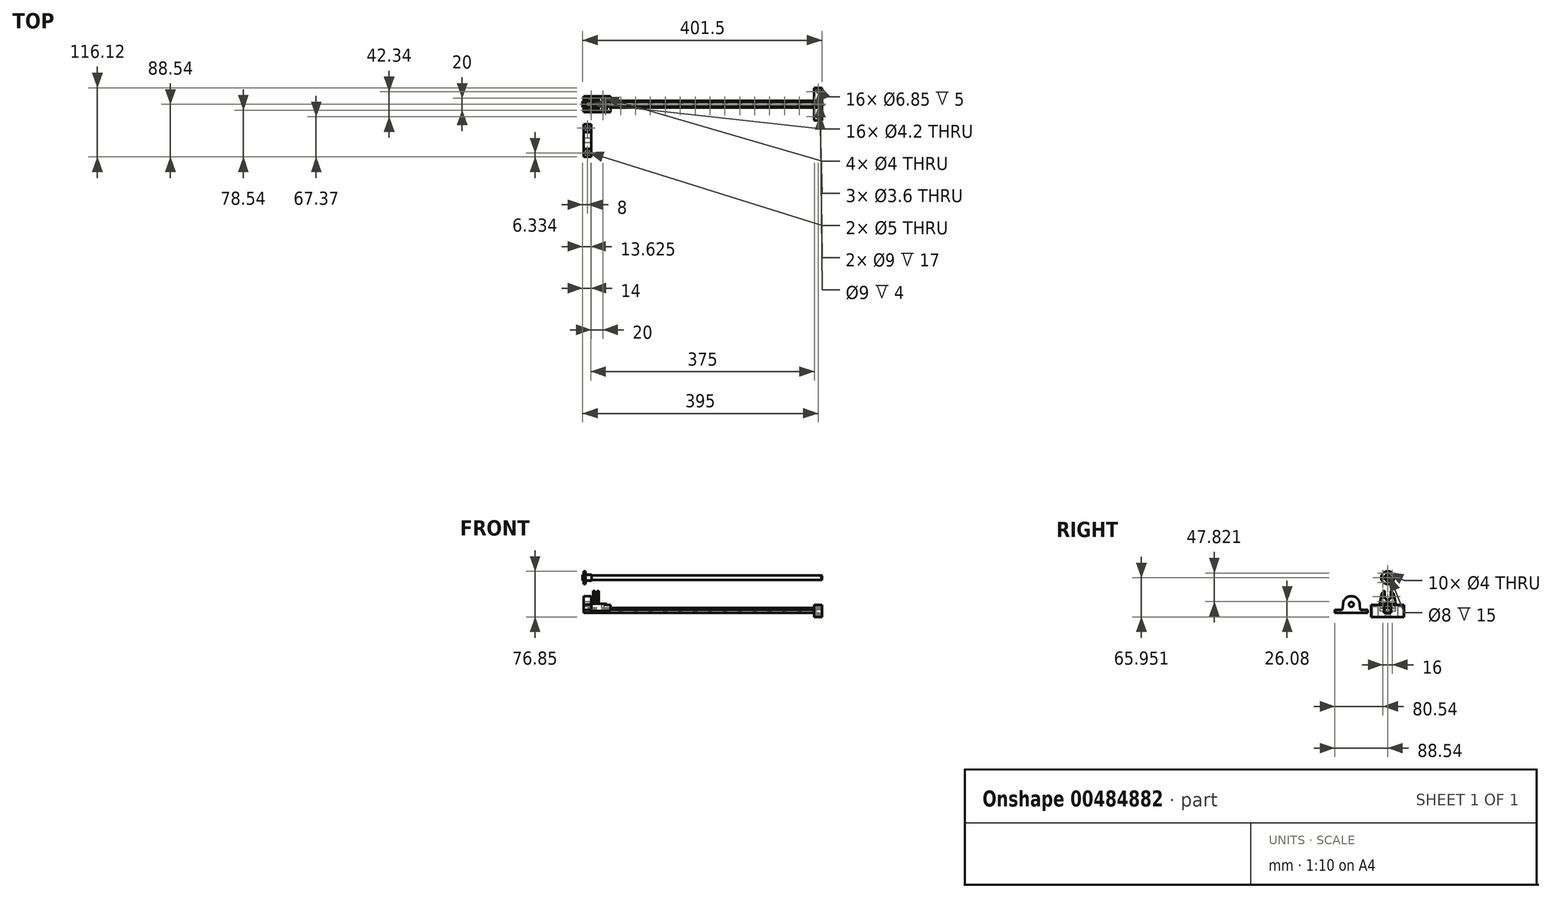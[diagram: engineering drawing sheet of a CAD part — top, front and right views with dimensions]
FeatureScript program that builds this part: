
annotation { "Feature Type Name" : "Feature", "Feature Type Description" : "" }
export const myFeature = defineFeature(function(context is Context, id is Id, definition is map)
    precondition{}
    {
        {
            var Q0;
            Q0=qCreatedBy(makeId("Right.planeOp"),FACE);
            var sketch = newSketch(context, id + "F0", { "sketchPlane" : qUnion([Q0])});
            skLineSegment(sketch, "E0.bottom", {"start": v(0, 0) * mm, "end": v(12, 0) * mm});
            skLineSegment(sketch, "E0.top", {"start": v(0, 8) * mm, "end": v(12, 8) * mm});
            skLineSegment(sketch, "E0.left", {"start": v(0, 0) * mm, "end": v(0, 8) * mm});
            skLineSegment(sketch, "E0.right", {"start": v(12, 0) * mm, "end": v(12, 8) * mm});
            skLineSegment(sketch, "E1", {"start": v(12, 0) * mm, "end": v(12, 3) * mm});
            skLineSegment(sketch, "E2", {"start": v(12, 3) * mm, "end": v(19.5, 3) * mm});
            skLineSegment(sketch, "E3", {"start": v(19.5, 3) * mm, "end": v(19.5, 13) * mm});
            skLineSegment(sketch, "E4", {"start": v(19.5, 13) * mm, "end": v(-7.5, 13) * mm});
            skLineSegment(sketch, "E5", {"start": v(-7.5, 13) * mm, "end": v(-7.5, 3) * mm});
            skLineSegment(sketch, "E6", {"start": v(-7.5, 3) * mm, "end": v(0, 3) * mm});
            skCircle(sketch, "E7", {"center": v(6, 58.87) * mm, "radius": 4 * mm});
            skCircle(sketch, "E8", {"center": v(6, 58.87) * mm, "radius": 10.9 * mm});
            skCircle(sketch, "E9", {"center": v(6, 58.87) * mm, "radius": 5 * mm});
            skLineSegment(sketch, "E10", {"start": v(1, 58.87) * mm, "end": v(-4.9, 58.87) * mm, "construction": true});
            skCircle(sketch, "E11", {"center": v(-1.95, 58.87) * mm, "radius": 2 * mm});
            skLineSegment(sketch, "E12", {"start": v(11, 58.87) * mm, "end": v(16.9, 58.87) * mm, "construction": true});
            skLineSegment(sketch, "E13", {"start": v(6, 53.87) * mm, "end": v(6, 47.97) * mm, "construction": true});
            skLineSegment(sketch, "E14", {"start": v(6, 63.87) * mm, "end": v(6, 69.77) * mm, "construction": true});
            skCircle(sketch, "E15", {"center": v(6, 66.82) * mm, "radius": 2 * mm});
            skCircle(sketch, "E16", {"center": v(13.95, 58.87) * mm, "radius": 2 * mm});
            skCircle(sketch, "E17", {"center": v(6, 50.92) * mm, "radius": 2 * mm});
            skLineSegment(sketch, "E18", {"start": v(-27.54, 0) * mm, "end": v(-82.54, 0) * mm});
            skLineSegment(sketch, "E19", {"start": v(-82.54, 0) * mm, "end": v(-82.54, 5) * mm});
            skLineSegment(sketch, "E20", {"start": v(-27.54, 0) * mm, "end": v(-27.54, 5) * mm});
            skLineSegment(sketch, "E21", {"start": v(-55.04, 0) * mm, "end": v(-55.04, 14) * mm, "construction": true});
            skPoint(sketch, "E21.endSnap0", {"position": v(-55.04, 0) * mm});
            skCircle(sketch, "E22", {"center": v(-55.04, 14) * mm, "radius": 14 * mm});
            skCircle(sketch, "E23", {"center": v(-55.04, 14) * mm, "radius": 4 * mm});
            skLineSegment(sketch, "E24", {"start": v(-40.2, 5) * mm, "end": v(-27.54, 5) * mm});
            skLineSegment(sketch, "E25", {"start": v(-69.88, 5) * mm, "end": v(-82.54, 5) * mm});
            skLineSegment(sketch, "E26", {"start": v(-41.04, 14) * mm, "end": v(-40.2, 5) * mm});
            skLineSegment(sketch, "E27", {"start": v(-69.04, 14) * mm, "end": v(-69.88, 5) * mm});
            skCircle(sketch, "E28", {"center": v(-55.04, 14) * mm, "radius": 5.9 * mm});
            skLineSegment(sketch, "E29", {"start": v(6, 0) * mm, "end": v(6, 58.87) * mm});
            skLineSegment(sketch, "E30", {"start": v(0, 6.36) * mm, "end": v(2, 5.52) * mm});
            skLineSegment(sketch, "E31", {"start": v(2, 5.52) * mm, "end": v(0, 4.68) * mm});
            skLineSegment(sketch, "E32.MirrorCS", {"start": v(12, 6.36) * mm, "end": v(10, 5.52) * mm});
            skLineSegment(sketch, "E33.MirrorCS", {"start": v(10, 5.52) * mm, "end": v(12, 4.68) * mm});
            skSolve(sketch);
        }
        {
            var Q0;
            {var subQ3=sQuery(id+"F0.wireOp",EDGE,"E0.bottom");Q0=makeQuery(id+"F0.imprint","IMPRINT",FACE,{"disambiguationData":[TD([[makeQuery(id+"F0.imprint","IMPRINT",EDGE,{"derivedFrom":subQ3}),1.0]])]});}
            extrude(context, id + "F1", {"entities" : qUnion([Q0]), "depth" : 400 * mm, "offsetDistance" : 25 * mm});
        }
        {
            var Q0;
            Q0=makeQuery(id+"F1.opExtrude","SWEPT_FACE",FACE,{"disambiguationData":[OSD([sQuery(id+"F0.wireOp",EDGE,"E0.top")])]});
            var sketch = newSketch(context, id + "F2", { "sketchPlane" : qUnion([Q0])});
            skLineSegment(sketch, "E34", {"start": v(0, 6) * mm, "end": v(12.12, 6) * mm, "construction": true});
            skCircle(sketch, "E35", {"center": v(12.12, 6) * mm, "radius": 3.43 * mm});
            skCircle(sketch, "E36", {"center": v(12.12, 6) * mm, "radius": 2.1 * mm});
            skCircle(sketch, "E37.1.0.0", {"center": v(37.13, 6) * mm, "radius": 2.1 * mm});
            skCircle(sketch, "E37.1.0.1", {"center": v(37.13, 6) * mm, "radius": 3.43 * mm});
            skCircle(sketch, "E37.2.0.0", {"center": v(62.13, 6) * mm, "radius": 2.1 * mm});
            skCircle(sketch, "E37.2.0.1", {"center": v(62.13, 6) * mm, "radius": 3.43 * mm});
            skCircle(sketch, "E37.3.0.0", {"center": v(87.13, 6) * mm, "radius": 2.1 * mm});
            skCircle(sketch, "E37.3.0.1", {"center": v(87.13, 6) * mm, "radius": 3.43 * mm});
            skCircle(sketch, "E37.4.0.0", {"center": v(112.13, 6) * mm, "radius": 2.1 * mm});
            skCircle(sketch, "E37.4.0.1", {"center": v(112.13, 6) * mm, "radius": 3.43 * mm});
            skCircle(sketch, "E37.5.0.0", {"center": v(137.13, 6) * mm, "radius": 2.1 * mm});
            skCircle(sketch, "E37.5.0.1", {"center": v(137.13, 6) * mm, "radius": 3.43 * mm});
            skCircle(sketch, "E37.6.0.0", {"center": v(162.13, 6) * mm, "radius": 2.1 * mm});
            skCircle(sketch, "E37.6.0.1", {"center": v(162.13, 6) * mm, "radius": 3.43 * mm});
            skCircle(sketch, "E37.7.0.0", {"center": v(187.13, 6) * mm, "radius": 2.1 * mm});
            skCircle(sketch, "E37.7.0.1", {"center": v(187.13, 6) * mm, "radius": 3.43 * mm});
            skCircle(sketch, "E37.8.0.0", {"center": v(212.13, 6) * mm, "radius": 2.1 * mm});
            skCircle(sketch, "E37.8.0.1", {"center": v(212.13, 6) * mm, "radius": 3.43 * mm});
            skCircle(sketch, "E37.9.0.0", {"center": v(237.13, 6) * mm, "radius": 2.1 * mm});
            skCircle(sketch, "E37.9.0.1", {"center": v(237.13, 6) * mm, "radius": 3.43 * mm});
            skCircle(sketch, "E37.10.0.0", {"center": v(262.13, 6) * mm, "radius": 2.1 * mm});
            skCircle(sketch, "E37.10.0.1", {"center": v(262.13, 6) * mm, "radius": 3.43 * mm});
            skCircle(sketch, "E37.11.0.0", {"center": v(287.13, 6) * mm, "radius": 2.1 * mm});
            skCircle(sketch, "E37.11.0.1", {"center": v(287.13, 6) * mm, "radius": 3.43 * mm});
            skCircle(sketch, "E37.12.0.0", {"center": v(312.13, 6) * mm, "radius": 2.1 * mm});
            skCircle(sketch, "E37.12.0.1", {"center": v(312.13, 6) * mm, "radius": 3.43 * mm});
            skCircle(sketch, "E37.13.0.0", {"center": v(337.13, 6) * mm, "radius": 2.1 * mm});
            skCircle(sketch, "E37.13.0.1", {"center": v(337.13, 6) * mm, "radius": 3.43 * mm});
            skCircle(sketch, "E37.14.0.0", {"center": v(362.13, 6) * mm, "radius": 2.1 * mm});
            skCircle(sketch, "E37.14.0.1", {"center": v(362.13, 6) * mm, "radius": 3.43 * mm});
            skCircle(sketch, "E37.15.0.0", {"center": v(387.13, 6) * mm, "radius": 2.1 * mm});
            skCircle(sketch, "E37.15.0.1", {"center": v(387.13, 6) * mm, "radius": 3.43 * mm});
            skLineSegment(sketch, "E37.direction1", {"start": v(12.12, 6) * mm, "end": v(37.13, 6) * mm, "construction": true});
            skLineSegment(sketch, "E38", {"start": v(112.13, 6) * mm, "end": v(87.13, 6) * mm});
            skSolve(sketch);
        }
        {
            var Q0;
            Q0=makeQuery(id+"F2.imprint","IMPRINT",FACE,{"disambiguationData":[TD([[makeQuery(id+"F2.imprint","IMPRINT",EDGE,{"derivedFrom":sQuery(id+"F2.wireOp",EDGE,"E35")}),1.0]])]});
            var Q1;
            Q1=makeQuery(id+"F2.imprint","IMPRINT",FACE,{"disambiguationData":[TD([[makeQuery(id+"F2.imprint","IMPRINT",EDGE,{"derivedFrom":sQuery(id+"F2.wireOp",EDGE,"E36")}),1.0]])]});
            var Q2;
            Q2=makeQuery(id+"F2.imprint","IMPRINT",FACE,{"disambiguationData":[TD([[makeQuery(id+"F2.imprint","IMPRINT",EDGE,{"derivedFrom":sQuery(id+"F2.wireOp",EDGE,"E37.1.0.0")}),1.0]])]});
            var Q3;
            Q3=makeQuery(id+"F2.imprint","IMPRINT",FACE,{"disambiguationData":[TD([[makeQuery(id+"F2.imprint","IMPRINT",EDGE,{"derivedFrom":sQuery(id+"F2.wireOp",EDGE,"E37.1.0.0")}),-1.0]])]});
            var Q4;
            Q4=makeQuery(id+"F2.imprint","IMPRINT",FACE,{"disambiguationData":[TD([[makeQuery(id+"F2.imprint","IMPRINT",EDGE,{"derivedFrom":sQuery(id+"F2.wireOp",EDGE,"E37.2.0.0")}),1.0]])]});
            var Q5;
            Q5=makeQuery(id+"F2.imprint","IMPRINT",FACE,{"disambiguationData":[TD([[makeQuery(id+"F2.imprint","IMPRINT",EDGE,{"derivedFrom":sQuery(id+"F2.wireOp",EDGE,"E37.2.0.0")}),-1.0]])]});
            var Q6;
            Q6=makeQuery(id+"F2.imprint","IMPRINT",FACE,{"disambiguationData":[TD([[makeQuery(id+"F2.imprint","IMPRINT",EDGE,{"derivedFrom":sQuery(id+"F2.wireOp",EDGE,"E37.3.0.0")}),1.0]])]});
            var Q7;
            Q7=makeQuery(id+"F2.imprint","IMPRINT",FACE,{"disambiguationData":[TD([[makeQuery(id+"F2.imprint","IMPRINT",EDGE,{"derivedFrom":sQuery(id+"F2.wireOp",EDGE,"E37.3.0.0")}),-1.0]])]});
            var Q8;
            Q8=makeQuery(id+"F2.imprint","IMPRINT",FACE,{"disambiguationData":[TD([[makeQuery(id+"F2.imprint","IMPRINT",EDGE,{"derivedFrom":sQuery(id+"F2.wireOp",EDGE,"E37.4.0.0")}),1.0]])]});
            var Q9;
            Q9=makeQuery(id+"F2.imprint","IMPRINT",FACE,{"disambiguationData":[TD([[makeQuery(id+"F2.imprint","IMPRINT",EDGE,{"derivedFrom":sQuery(id+"F2.wireOp",EDGE,"E37.4.0.0")}),-1.0]])]});
            var Q10;
            Q10=makeQuery(id+"F2.imprint","IMPRINT",FACE,{"disambiguationData":[TD([[makeQuery(id+"F2.imprint","IMPRINT",EDGE,{"derivedFrom":sQuery(id+"F2.wireOp",EDGE,"E37.5.0.0")}),1.0]])]});
            var Q11;
            Q11=makeQuery(id+"F2.imprint","IMPRINT",FACE,{"disambiguationData":[TD([[makeQuery(id+"F2.imprint","IMPRINT",EDGE,{"derivedFrom":sQuery(id+"F2.wireOp",EDGE,"E37.5.0.0")}),-1.0]])]});
            var Q12;
            Q12=makeQuery(id+"F2.imprint","IMPRINT",FACE,{"disambiguationData":[TD([[makeQuery(id+"F2.imprint","IMPRINT",EDGE,{"derivedFrom":sQuery(id+"F2.wireOp",EDGE,"E37.6.0.0")}),1.0]])]});
            var Q13;
            Q13=makeQuery(id+"F2.imprint","IMPRINT",FACE,{"disambiguationData":[TD([[makeQuery(id+"F2.imprint","IMPRINT",EDGE,{"derivedFrom":sQuery(id+"F2.wireOp",EDGE,"E37.6.0.0")}),-1.0]])]});
            var Q14;
            Q14=makeQuery(id+"F2.imprint","IMPRINT",FACE,{"disambiguationData":[TD([[makeQuery(id+"F2.imprint","IMPRINT",EDGE,{"derivedFrom":sQuery(id+"F2.wireOp",EDGE,"E37.7.0.0")}),1.0]])]});
            var Q15;
            Q15=makeQuery(id+"F2.imprint","IMPRINT",FACE,{"disambiguationData":[TD([[makeQuery(id+"F2.imprint","IMPRINT",EDGE,{"derivedFrom":sQuery(id+"F2.wireOp",EDGE,"E37.7.0.0")}),-1.0]])]});
            var Q16;
            Q16=makeQuery(id+"F2.imprint","IMPRINT",FACE,{"disambiguationData":[TD([[makeQuery(id+"F2.imprint","IMPRINT",EDGE,{"derivedFrom":sQuery(id+"F2.wireOp",EDGE,"E37.15.0.0")}),1.0]])]});
            var Q17;
            Q17=makeQuery(id+"F2.imprint","IMPRINT",FACE,{"disambiguationData":[TD([[makeQuery(id+"F2.imprint","IMPRINT",EDGE,{"derivedFrom":sQuery(id+"F2.wireOp",EDGE,"E37.15.0.0")}),-1.0]])]});
            var Q18;
            Q18=makeQuery(id+"F2.imprint","IMPRINT",FACE,{"disambiguationData":[TD([[makeQuery(id+"F2.imprint","IMPRINT",EDGE,{"derivedFrom":sQuery(id+"F2.wireOp",EDGE,"E37.14.0.0")}),1.0]])]});
            var Q19;
            Q19=makeQuery(id+"F2.imprint","IMPRINT",FACE,{"disambiguationData":[TD([[makeQuery(id+"F2.imprint","IMPRINT",EDGE,{"derivedFrom":sQuery(id+"F2.wireOp",EDGE,"E37.14.0.0")}),-1.0]])]});
            var Q20;
            Q20=makeQuery(id+"F2.imprint","IMPRINT",FACE,{"disambiguationData":[TD([[makeQuery(id+"F2.imprint","IMPRINT",EDGE,{"derivedFrom":sQuery(id+"F2.wireOp",EDGE,"E37.13.0.0")}),1.0]])]});
            var Q21;
            Q21=makeQuery(id+"F2.imprint","IMPRINT",FACE,{"disambiguationData":[TD([[makeQuery(id+"F2.imprint","IMPRINT",EDGE,{"derivedFrom":sQuery(id+"F2.wireOp",EDGE,"E37.13.0.0")}),-1.0]])]});
            var Q22;
            Q22=makeQuery(id+"F2.imprint","IMPRINT",FACE,{"disambiguationData":[TD([[makeQuery(id+"F2.imprint","IMPRINT",EDGE,{"derivedFrom":sQuery(id+"F2.wireOp",EDGE,"E37.12.0.0")}),1.0]])]});
            var Q23;
            Q23=makeQuery(id+"F2.imprint","IMPRINT",FACE,{"disambiguationData":[TD([[makeQuery(id+"F2.imprint","IMPRINT",EDGE,{"derivedFrom":sQuery(id+"F2.wireOp",EDGE,"E37.12.0.0")}),-1.0]])]});
            var Q24;
            Q24=makeQuery(id+"F2.imprint","IMPRINT",FACE,{"disambiguationData":[TD([[makeQuery(id+"F2.imprint","IMPRINT",EDGE,{"derivedFrom":sQuery(id+"F2.wireOp",EDGE,"E37.11.0.0")}),1.0]])]});
            var Q25;
            Q25=makeQuery(id+"F2.imprint","IMPRINT",FACE,{"disambiguationData":[TD([[makeQuery(id+"F2.imprint","IMPRINT",EDGE,{"derivedFrom":sQuery(id+"F2.wireOp",EDGE,"E37.11.0.0")}),-1.0]])]});
            var Q26;
            Q26=makeQuery(id+"F2.imprint","IMPRINT",FACE,{"disambiguationData":[TD([[makeQuery(id+"F2.imprint","IMPRINT",EDGE,{"derivedFrom":sQuery(id+"F2.wireOp",EDGE,"E37.10.0.0")}),1.0]])]});
            var Q27;
            Q27=makeQuery(id+"F2.imprint","IMPRINT",FACE,{"disambiguationData":[TD([[makeQuery(id+"F2.imprint","IMPRINT",EDGE,{"derivedFrom":sQuery(id+"F2.wireOp",EDGE,"E37.10.0.0")}),-1.0]])]});
            var Q28;
            Q28=makeQuery(id+"F2.imprint","IMPRINT",FACE,{"disambiguationData":[TD([[makeQuery(id+"F2.imprint","IMPRINT",EDGE,{"derivedFrom":sQuery(id+"F2.wireOp",EDGE,"E37.9.0.0")}),1.0]])]});
            var Q29;
            Q29=makeQuery(id+"F2.imprint","IMPRINT",FACE,{"disambiguationData":[TD([[makeQuery(id+"F2.imprint","IMPRINT",EDGE,{"derivedFrom":sQuery(id+"F2.wireOp",EDGE,"E37.9.0.0")}),-1.0]])]});
            var Q30;
            Q30=makeQuery(id+"F2.imprint","IMPRINT",FACE,{"disambiguationData":[TD([[makeQuery(id+"F2.imprint","IMPRINT",EDGE,{"derivedFrom":sQuery(id+"F2.wireOp",EDGE,"E37.8.0.0")}),1.0]])]});
            var Q31;
            Q31=makeQuery(id+"F2.imprint","IMPRINT",FACE,{"disambiguationData":[TD([[makeQuery(id+"F2.imprint","IMPRINT",EDGE,{"derivedFrom":sQuery(id+"F2.wireOp",EDGE,"E37.8.0.0")}),-1.0]])]});
            extrude(context, id + "F3", {"entities" : qUnion([Q0, Q1, Q2, Q3, Q4, Q5, Q6, Q7, Q8, Q9, Q10, Q11, Q12, Q13, Q14, Q15, Q16, Q17, Q18, Q19, Q20, Q21, Q22, Q23, Q24, Q25, Q26, Q27, Q28, Q29, Q30, Q31]), "operationType" : NewBodyOperationType.REMOVE, "oppositeDirection" : true, "depth" : 5 * mm, "offsetDistance" : 25 * mm});
        }
        {
            var Q0;
            Q0=makeQuery(id+"F2.imprint","IMPRINT",FACE,{"disambiguationData":[TD([[makeQuery(id+"F2.imprint","IMPRINT",EDGE,{"derivedFrom":sQuery(id+"F2.wireOp",EDGE,"E36")}),1.0]])]});
            var Q1;
            Q1=makeQuery(id+"F2.imprint","IMPRINT",FACE,{"disambiguationData":[TD([[makeQuery(id+"F2.imprint","IMPRINT",EDGE,{"derivedFrom":sQuery(id+"F2.wireOp",EDGE,"E37.1.0.0")}),1.0]])]});
            var Q2;
            Q2=makeQuery(id+"F2.imprint","IMPRINT",FACE,{"disambiguationData":[TD([[makeQuery(id+"F2.imprint","IMPRINT",EDGE,{"derivedFrom":sQuery(id+"F2.wireOp",EDGE,"E37.2.0.0")}),1.0]])]});
            var Q3;
            Q3=makeQuery(id+"F2.imprint","IMPRINT",FACE,{"disambiguationData":[TD([[makeQuery(id+"F2.imprint","IMPRINT",EDGE,{"derivedFrom":sQuery(id+"F2.wireOp",EDGE,"E37.3.0.0")}),1.0]])]});
            var Q4;
            Q4=makeQuery(id+"F2.imprint","IMPRINT",FACE,{"disambiguationData":[TD([[makeQuery(id+"F2.imprint","IMPRINT",EDGE,{"derivedFrom":sQuery(id+"F2.wireOp",EDGE,"E37.4.0.0")}),1.0]])]});
            var Q5;
            Q5=makeQuery(id+"F2.imprint","IMPRINT",FACE,{"disambiguationData":[TD([[makeQuery(id+"F2.imprint","IMPRINT",EDGE,{"derivedFrom":sQuery(id+"F2.wireOp",EDGE,"E37.5.0.0")}),1.0]])]});
            var Q6;
            Q6=makeQuery(id+"F2.imprint","IMPRINT",FACE,{"disambiguationData":[TD([[makeQuery(id+"F2.imprint","IMPRINT",EDGE,{"derivedFrom":sQuery(id+"F2.wireOp",EDGE,"E37.6.0.0")}),1.0]])]});
            var Q7;
            Q7=makeQuery(id+"F2.imprint","IMPRINT",FACE,{"disambiguationData":[TD([[makeQuery(id+"F2.imprint","IMPRINT",EDGE,{"derivedFrom":sQuery(id+"F2.wireOp",EDGE,"E37.7.0.0")}),1.0]])]});
            var Q8;
            Q8=makeQuery(id+"F2.imprint","IMPRINT",FACE,{"disambiguationData":[TD([[makeQuery(id+"F2.imprint","IMPRINT",EDGE,{"derivedFrom":sQuery(id+"F2.wireOp",EDGE,"E37.8.0.0")}),1.0]])]});
            var Q9;
            Q9=makeQuery(id+"F2.imprint","IMPRINT",FACE,{"disambiguationData":[TD([[makeQuery(id+"F2.imprint","IMPRINT",EDGE,{"derivedFrom":sQuery(id+"F2.wireOp",EDGE,"E37.9.0.0")}),1.0]])]});
            var Q10;
            Q10=makeQuery(id+"F2.imprint","IMPRINT",FACE,{"disambiguationData":[TD([[makeQuery(id+"F2.imprint","IMPRINT",EDGE,{"derivedFrom":sQuery(id+"F2.wireOp",EDGE,"E37.10.0.0")}),1.0]])]});
            var Q11;
            Q11=makeQuery(id+"F2.imprint","IMPRINT",FACE,{"disambiguationData":[TD([[makeQuery(id+"F2.imprint","IMPRINT",EDGE,{"derivedFrom":sQuery(id+"F2.wireOp",EDGE,"E37.11.0.0")}),1.0]])]});
            var Q12;
            Q12=makeQuery(id+"F2.imprint","IMPRINT",FACE,{"disambiguationData":[TD([[makeQuery(id+"F2.imprint","IMPRINT",EDGE,{"derivedFrom":sQuery(id+"F2.wireOp",EDGE,"E37.12.0.0")}),1.0]])]});
            var Q13;
            Q13=makeQuery(id+"F2.imprint","IMPRINT",FACE,{"disambiguationData":[TD([[makeQuery(id+"F2.imprint","IMPRINT",EDGE,{"derivedFrom":sQuery(id+"F2.wireOp",EDGE,"E37.13.0.0")}),1.0]])]});
            var Q14;
            Q14=makeQuery(id+"F2.imprint","IMPRINT",FACE,{"disambiguationData":[TD([[makeQuery(id+"F2.imprint","IMPRINT",EDGE,{"derivedFrom":sQuery(id+"F2.wireOp",EDGE,"E37.14.0.0")}),1.0]])]});
            var Q15;
            Q15=makeQuery(id+"F2.imprint","IMPRINT",FACE,{"disambiguationData":[TD([[makeQuery(id+"F2.imprint","IMPRINT",EDGE,{"derivedFrom":sQuery(id+"F2.wireOp",EDGE,"E37.15.0.0")}),1.0]])]});
            var Q16;
            Q16=makeQuery(id+"F1.opExtrude","SWEPT_FACE",FACE,{"disambiguationData":[OSD([sQuery(id+"F0.wireOp",EDGE,"E0.bottom")])]});
            extrude(context, id + "F4", {"entities" : qUnion([Q0, Q1, Q2, Q3, Q4, Q5, Q6, Q7, Q8, Q9, Q10, Q11, Q12, Q13, Q14, Q15]), "operationType" : NewBodyOperationType.REMOVE, "endBound" : BoundingType.UP_TO_SURFACE, "oppositeDirection" : true, "depth" : 25 * mm, "endBoundEntityFace" : qUnion([Q16]), "offsetDistance" : 25 * mm});
        }
        {
            var Q0;
            {var subQ1=sQuery(id+"F0.wireOp",EDGE,"E0.top");Q0=makeQuery(id+"F0.imprint","IMPRINT",FACE,{"disambiguationData":[TD([[makeQuery(id+"F0.imprint","IMPRINT",EDGE,{"derivedFrom":subQ1}),1.0]])]});}
            var Q1;
            {var subQ0=sQuery(id+"F0.wireOp",EDGE,"E30");Q1=makeQuery(id+"F0.imprint","IMPRINT",FACE,{"disambiguationData":[TD([[makeQuery(id+"F0.imprint","IMPRINT",EDGE,{"derivedFrom":subQ0}),-1.0]])]});}
            var Q2;
            {var subQ0=sQuery(id+"F0.wireOp",EDGE,"E32.MirrorCS");Q2=makeQuery(id+"F0.imprint","IMPRINT",FACE,{"disambiguationData":[TD([[makeQuery(id+"F0.imprint","IMPRINT",EDGE,{"derivedFrom":subQ0}),1.0]])]});}
            extrude(context, id + "F5", {"entities" : qUnion([Q0, Q1, Q2]), "depth" : 45 * mm, "offsetDistance" : 25 * mm});
        }
        {
            var Q0;
            Q0=makeQuery(id+"F5.opExtrude","SWEPT_FACE",FACE,{"disambiguationData":[OSD([sQuery(id+"F0.wireOp",EDGE,"E4")])]});
            var sketch = newSketch(context, id + "F6", { "sketchPlane" : qUnion([Q0])});
            skLineSegment(sketch, "E39", {"start": v(11.25, 19.5) * mm, "end": v(12.5, 19.5) * mm});
            skLineSegment(sketch, "E40", {"start": v(12.5, 19.5) * mm, "end": v(12.5, 16) * mm, "construction": true});
            skLineSegment(sketch, "E41", {"start": v(12.5, 16) * mm, "end": v(32.5, 16) * mm, "construction": true});
            skLineSegment(sketch, "E42", {"start": v(32.5, 16) * mm, "end": v(32.5, -4) * mm, "construction": true});
            skLineSegment(sketch, "E43", {"start": v(32.5, -4) * mm, "end": v(12.5, -4) * mm, "construction": true});
            skLineSegment(sketch, "E44", {"start": v(32.5, 16) * mm, "end": v(45, 16) * mm});
            skCircle(sketch, "E45", {"center": v(12.5, 16) * mm, "radius": 2 * mm});
            skCircle(sketch, "E46", {"center": v(32.5, 16) * mm, "radius": 2 * mm});
            skCircle(sketch, "E47", {"center": v(32.5, -4) * mm, "radius": 2 * mm});
            skCircle(sketch, "E48", {"center": v(12.5, -4) * mm, "radius": 2 * mm});
            skLineSegment(sketch, "E49", {"start": v(6.25, 14.5) * mm, "end": v(6.25, -2.5) * mm});
            skLineSegment(sketch, "E50", {"start": v(38.75, 14.5) * mm, "end": v(38.75, -2.5) * mm});
            skPoint(sketch, "E50.startSnap0", {"position": v(38.75, 16) * mm});
            skLineSegment(sketch, "E51", {"start": v(33.75, 19.5) * mm, "end": v(12.5, 19.5) * mm});
            skLineSegment(sketch, "E52", {"start": v(33.75, -7.5) * mm, "end": v(11.25, -7.5) * mm});
            skPoint(sketch, "E53.newPointA", {"position": v(6.25, 19.5) * mm});
            skPoint(sketch, "E53.newPointB", {"position": v(0, 19.5) * mm});
            skArc(sketch, "E53.filletArc", {"start": v(11.25, 19.5) * mm, "mid": v(7.71, 18.04) * mm, "end": v(6.25, 14.5) * mm});
            skPoint(sketch, "E54.visualSharp", {"position": v(6.25, -7.5) * mm});
            skArc(sketch, "E54.filletArc", {"start": v(6.25, -2.5) * mm, "mid": v(7.71, -6.04) * mm, "end": v(11.25, -7.5) * mm});
            skPoint(sketch, "E55.visualSharp", {"position": v(38.75, -7.5) * mm});
            skArc(sketch, "E55.filletArc", {"start": v(33.75, -7.5) * mm, "mid": v(37.29, -6.04) * mm, "end": v(38.75, -2.5) * mm});
            skPoint(sketch, "E56.visualSharp", {"position": v(38.75, 19.5) * mm});
            skArc(sketch, "E56.filletArc", {"start": v(38.75, 14.5) * mm, "mid": v(37.29, 18.04) * mm, "end": v(33.75, 19.5) * mm});
            skLineSegment(sketch, "E57", {"start": v(16.25, 19.5) * mm, "end": v(16.25, -7.5) * mm});
            skLineSegment(sketch, "E58", {"start": v(19.25, 19.5) * mm, "end": v(19.25, -7.5) * mm});
            skLineSegment(sketch, "E59", {"start": v(25.75, 19.5) * mm, "end": v(25.75, -7.5) * mm});
            skLineSegment(sketch, "E60", {"start": v(22.75, -7.5) * mm, "end": v(22.75, 19.5) * mm});
            skLineSegment(sketch, "E61", {"start": v(19.25, 6) * mm, "end": v(22.75, 6) * mm, "construction": true});
            skLineSegment(sketch, "E62", {"start": v(19.25, 6) * mm, "end": v(16.25, 6) * mm, "construction": true});
            skLineSegment(sketch, "E63", {"start": v(22.75, 6) * mm, "end": v(25.75, 6) * mm, "construction": true});
            skLineSegment(sketch, "E64", {"start": v(16.25, 6) * mm, "end": v(6.25, 6) * mm, "construction": true});
            skSolve(sketch);
        }
        {
            var Q0;
            Q0=sQuery(id+"F6.wireOp",VERTEX,"E41.start");
            var Q1;
            Q1=sQuery(id+"F6.wireOp",VERTEX,"E42.start");
            var Q2;
            Q2=sQuery(id+"F6.wireOp",VERTEX,"E42.end");
            var Q3;
            Q3=sQuery(id+"F6.wireOp",VERTEX,"E43.end");
            var Q4;
            Q4=makeQuery(id+"F5.opExtrude","SWEPT_BODY",BODY,{"disambiguationData":[OSD([sQuery(id+"F0.wireOp",EDGE,"E0.top"),sQuery(id+"F0.wireOp",EDGE,"E0.left"),sQuery(id+"F0.wireOp",EDGE,"E0.right"),sQuery(id+"F0.wireOp",EDGE,"E2"),sQuery(id+"F0.wireOp",EDGE,"E3"),sQuery(id+"F0.wireOp",EDGE,"E4"),sQuery(id+"F0.wireOp",EDGE,"E5"),sQuery(id+"F0.wireOp",EDGE,"E6")])]});
            hole(context, id + "F7", {"style" : HoleStyle.SIMPLE, "endStyle" : HoleEndStyle.BLIND, "holeDiameter" : 4 * mm, "majorDiameter" : 5 * mm, "holeDepth" : 5 * mm, "isTappedThrough" : true, "tappedDepth" : 12 * mm, "tapClearance" : 3, "locations" : qUnion([Q0, Q1, Q2, Q3]), "scope" : qUnion([Q4])});
        }
        {
            var Q0;
            Q0 = qSketchRegion(id + "F6", true);
            extrude(context, id + "F8", {"entities" : qUnion([Q0]), "depth" : 2 * mm, "offsetDistance" : 25 * mm});
        }
        {
            var Q0;
            {var subQ0=sQuery(id+"F6.wireOp",EDGE,"E59");Q0=makeQuery(id+"F6.imprint","IMPRINT",FACE,{"disambiguationData":[TD([[makeQuery(id+"F6.imprint","IMPRINT",EDGE,{"derivedFrom":subQ0}),-1.0]])]});}
            var Q1;
            {var subQ0=sQuery(id+"F6.wireOp",EDGE,"E57");Q1=makeQuery(id+"F6.imprint","IMPRINT",FACE,{"disambiguationData":[TD([[makeQuery(id+"F6.imprint","IMPRINT",EDGE,{"derivedFrom":subQ0}),1.0]])]});}
            extrude(context, id + "F9", {"entities" : qUnion([Q0, Q1]), "operationType" : NewBodyOperationType.ADD, "depth" : 26 * mm, "offsetDistance" : 25 * mm});
        }
        {
            var Q0;
            Q0=makeQuery(id+"F9.opExtrude","SWEPT_FACE",FACE,{"disambiguationData":[OSD([sQuery(id+"F6.wireOp",EDGE,"E59")])]});
            var sketch = newSketch(context, id + "F10", { "sketchPlane" : qUnion([Q0])});
            skLineSegment(sketch, "E65", {"start": v(6, 15) * mm, "end": v(6, 27) * mm, "construction": true});
            skCircle(sketch, "E66", {"center": v(6, 27) * mm, "radius": 5 * mm});
            skCircle(sketch, "E67", {"center": v(6, 27) * mm, "radius": 11 * mm});
            skLineSegment(sketch, "E68", {"start": v(1, 27) * mm, "end": v(1, 39) * mm});
            skLineSegment(sketch, "E69", {"start": v(11, 27) * mm, "end": v(11, 39) * mm});
            skLineSegment(sketch, "E70", {"start": v(-7.5, 15) * mm, "end": v(-4.8, 29.07) * mm});
            skLineSegment(sketch, "E71", {"start": v(19.5, 15) * mm, "end": v(16.8, 29.07) * mm});
            skLineSegment(sketch, "E72", {"start": v(1, 27) * mm, "end": v(-5, 27) * mm, "construction": true});
            skLineSegment(sketch, "E73", {"start": v(11, 27) * mm, "end": v(17, 27) * mm, "construction": true});
            skLineSegment(sketch, "E74", {"start": v(6, 22) * mm, "end": v(6, 16) * mm, "construction": true});
            skLineSegment(sketch, "E75", {"start": v(6, 32) * mm, "end": v(6, 38) * mm, "construction": true});
            skCircle(sketch, "E76", {"center": v(-2, 27) * mm, "radius": 2 * mm});
            skCircle(sketch, "E77", {"center": v(6, 35) * mm, "radius": 2 * mm});
            skCircle(sketch, "E78", {"center": v(6, 19) * mm, "radius": 2 * mm});
            skCircle(sketch, "E79", {"center": v(14, 27) * mm, "radius": 2 * mm});
            skSolve(sketch);
        }
        {
            var Q0;
            {var subQ0=sQuery(id+"F10.wireOp",EDGE,"E68");var subQ1=sQuery(id+"F10.wireOp",EDGE,"E66");var subQ2=makeQuery(id+"F10.imprint","INTERSECT",VERTEX,{"derivedFrom":[subQ1,subQ0]});Q0=makeQuery(id+"F10.imprint","IMPRINT",FACE,{"disambiguationData":[TD([[makeQuery(id+"F10.imprint","IMPRINT",EDGE,{"disambiguationData":[TD([[subQ2,1.0]])],"derivedFrom":subQ1}),-1.0]])]});}
            var Q1;
            {var subQ0=sQuery(id+"F10.wireOp",EDGE,"E68");var subQ1=sQuery(id+"F10.wireOp",EDGE,"E67");var subQ2=makeQuery(id+"F10.imprint","INTERSECT",VERTEX,{"derivedFrom":[subQ1,subQ0]});Q1=makeQuery(id+"F10.imprint","IMPRINT",FACE,{"disambiguationData":[TD([[makeQuery(id+"F10.imprint","IMPRINT",EDGE,{"disambiguationData":[TD([[subQ2,1.0]])],"derivedFrom":subQ1}),-1.0]])]});}
            var Q2;
            {var subQ0=sQuery(id+"F10.wireOp",EDGE,"E66");var subQ1=makeQuery(id+"F10.imprint","INTERSECT",VERTEX,{"derivedFrom":[subQ0,sQuery(id+"F10.wireOp",EDGE,"E68")]});Q2=makeQuery(id+"F10.imprint","IMPRINT",FACE,{"disambiguationData":[TD([[makeQuery(id+"F10.imprint","IMPRINT",EDGE,{"disambiguationData":[TD([[subQ1,1.0]])],"derivedFrom":subQ0}),1.0]])]});}
            var Q3;
            {var subQ2=sQuery(id+"F10.wireOp",EDGE,"E70");Q3=makeQuery(id+"F10.imprint","IMPRINT",FACE,{"disambiguationData":[TD([[makeQuery(id+"F10.imprint","IMPRINT",EDGE,{"derivedFrom":subQ2}),1.0]])]});}
            var Q4;
            {var subQ0=sQuery(id+"F10.wireOp",EDGE,"E71");Q4=makeQuery(id+"F10.imprint","IMPRINT",FACE,{"disambiguationData":[TD([[makeQuery(id+"F10.imprint","IMPRINT",EDGE,{"derivedFrom":subQ0}),-1.0]])]});}
            var Q5;
            Q5=makeQuery(id+"F10.imprint","IMPRINT",FACE,{"disambiguationData":[TD([[makeQuery(id+"F10.imprint","IMPRINT",EDGE,{"derivedFrom":sQuery(id+"F10.wireOp",EDGE,"E77")}),1.0]])]});
            var Q6;
            Q6=makeQuery(id+"F10.imprint","IMPRINT",FACE,{"disambiguationData":[TD([[makeQuery(id+"F10.imprint","IMPRINT",EDGE,{"derivedFrom":sQuery(id+"F10.wireOp",EDGE,"E79")}),1.0]])]});
            var Q7;
            Q7=makeQuery(id+"F10.imprint","IMPRINT",FACE,{"disambiguationData":[TD([[makeQuery(id+"F10.imprint","IMPRINT",EDGE,{"derivedFrom":sQuery(id+"F10.wireOp",EDGE,"E78")}),1.0]])]});
            var Q8;
            Q8=makeQuery(id+"F10.imprint","IMPRINT",FACE,{"disambiguationData":[TD([[makeQuery(id+"F10.imprint","IMPRINT",EDGE,{"derivedFrom":sQuery(id+"F10.wireOp",EDGE,"E76")}),1.0]])]});
            var Q9;
            Q9=makeQuery(id+"F9.opExtrude","SWEPT_FACE",FACE,{"disambiguationData":[OSD([sQuery(id+"F6.wireOp",EDGE,"E57")])]});
            extrude(context, id + "F11", {"entities" : qUnion([Q0, Q1, Q2, Q3, Q4, Q5, Q6, Q7, Q8]), "operationType" : NewBodyOperationType.REMOVE, "endBound" : BoundingType.UP_TO_SURFACE, "oppositeDirection" : true, "depth" : 25 * mm, "endBoundEntityFace" : qUnion([Q9]), "offsetDistance" : 25 * mm});
        }
        {
            var Q0;
            Q0=makeQuery(id+"F0.imprint","IMPRINT",FACE,{"disambiguationData":[TD([[makeQuery(id+"F0.imprint","IMPRINT",EDGE,{"derivedFrom":sQuery(id+"F0.wireOp",EDGE,"E7")}),-1.0]])]});
            extrude(context, id + "F12", {"entities" : qUnion([Q0]), "oppositeDirection" : true, "depth" : 1.5 * mm, "offsetDistance" : 25 * mm});
        }
        {
            var Q0;
            Q0=makeQuery(id+"F0.imprint","IMPRINT",FACE,{"disambiguationData":[TD([[makeQuery(id+"F0.imprint","IMPRINT",EDGE,{"derivedFrom":sQuery(id+"F0.wireOp",EDGE,"E7")}),-1.0]])]});
            extrude(context, id + "F13", {"entities" : qUnion([Q0]), "operationType" : NewBodyOperationType.ADD, "depth" : 13.5 * mm, "offsetDistance" : 25 * mm});
        }
        {
            var Q0;
            Q0=makeQuery(id+"F0.imprint","IMPRINT",FACE,{"disambiguationData":[TD([[makeQuery(id+"F0.imprint","IMPRINT",EDGE,{"derivedFrom":sQuery(id+"F0.wireOp",EDGE,"E8")}),1.0]])]});
            extrude(context, id + "F14", {"entities" : qUnion([Q0]), "operationType" : NewBodyOperationType.ADD, "depth" : 3.5 * mm, "offsetDistance" : 25 * mm});
        }
        {
            var Q0;
            Q0=makeQuery(id+"F0.imprint","IMPRINT",FACE,{"disambiguationData":[TD([[makeQuery(id+"F0.imprint","IMPRINT",EDGE,{"derivedFrom":sQuery(id+"F0.wireOp",EDGE,"E7")}),1.0]])]});
            extrude(context, id + "F15", {"entities" : qUnion([Q0]), "depth" : 400 * mm, "offsetDistance" : 25 * mm});
        }
        {
            var Q0;
            {var subQ4=sQuery(id+"F0.wireOp",EDGE,"E20");Q0=makeQuery(id+"F0.imprint","IMPRINT",FACE,{"disambiguationData":[TD([[makeQuery(id+"F0.imprint","IMPRINT",EDGE,{"derivedFrom":subQ4}),1.0]])]});}
            var Q1;
            {var subQ4=sQuery(id+"F0.wireOp",EDGE,"E19");Q1=makeQuery(id+"F0.imprint","IMPRINT",FACE,{"disambiguationData":[TD([[makeQuery(id+"F0.imprint","IMPRINT",EDGE,{"derivedFrom":subQ4}),-1.0]])]});}
            var Q2;
            Q2=makeQuery(id+"F0.imprint","IMPRINT",FACE,{"disambiguationData":[TD([[makeQuery(id+"F0.imprint","IMPRINT",EDGE,{"derivedFrom":sQuery(id+"F0.wireOp",EDGE,"E28")}),-1.0]])]});
            var Q3;
            Q3=makeQuery(id+"F0.imprint","IMPRINT",FACE,{"disambiguationData":[TD([[makeQuery(id+"F0.imprint","IMPRINT",EDGE,{"derivedFrom":sQuery(id+"F0.wireOp",EDGE,"E23")}),-1.0]])]});
            extrude(context, id + "F16", {"entities" : qUnion([Q0, Q1, Q2, Q3]), "depth" : 13 * mm, "offsetDistance" : 25 * mm});
        }
        {
            var Q0;
            Q0=makeQuery(id+"F16.opExtrude","SWEPT_FACE",FACE,{"disambiguationData":[OSD([sQuery(id+"F0.wireOp",EDGE,"E24")])]});
            var sketch = newSketch(context, id + "F17", { "sketchPlane" : qUnion([Q0])});
            skLineSegment(sketch, "E80", {"start": v(6.5, -27.54) * mm, "end": v(6.5, -40.2) * mm, "construction": true});
            skLineSegment(sketch, "E81", {"start": v(6.5, -33.87) * mm, "end": v(13, -33.87) * mm, "construction": true});
            skSolve(sketch);
        }
        {
            var Q0;
            Q0=makeQuery(id+"F16.opExtrude","SWEPT_FACE",FACE,{"disambiguationData":[OSD([sQuery(id+"F0.wireOp",EDGE,"E25")])]});
            var sketch = newSketch(context, id + "F18", { "sketchPlane" : qUnion([Q0])});
            skLineSegment(sketch, "E82", {"start": v(6.5, -69.88) * mm, "end": v(6.5, -82.54) * mm});
            skLineSegment(sketch, "E83", {"start": v(6.5, -76.2) * mm, "end": v(13, -76.2) * mm});
            skSolve(sketch);
        }
        {
            var Q0;
            Q0=sQuery(id+"F18.wireOp",VERTEX,"E83.start");
            var Q1;
            Q1=sQuery(id+"F17.wireOp",VERTEX,"E81.start");
            var Q2;
            Q2=makeQuery(id+"F16.opExtrude","SWEPT_BODY",BODY,{"disambiguationData":[OSD([sQuery(id+"F0.wireOp",EDGE,"E18"),sQuery(id+"F0.wireOp",EDGE,"E19"),sQuery(id+"F0.wireOp",EDGE,"E20"),sQuery(id+"F0.wireOp",EDGE,"E22"),sQuery(id+"F0.wireOp",EDGE,"E23"),sQuery(id+"F0.wireOp",EDGE,"E24"),sQuery(id+"F0.wireOp",EDGE,"E25"),sQuery(id+"F0.wireOp",EDGE,"E26"),sQuery(id+"F0.wireOp",EDGE,"E27")])]});
            hole(context, id + "F19", {"style" : HoleStyle.SIMPLE, "endStyle" : HoleEndStyle.BLIND, "holeDiameter" : 5 * mm, "majorDiameter" : 5 * mm, "holeDepth" : 5 * mm, "isTappedThrough" : true, "tappedDepth" : 12 * mm, "tapClearance" : 3, "locations" : qUnion([Q0, Q1]), "scope" : qUnion([Q2])});
        }
        {
            var Q0;
            Q0=sQuery(id+"F0.wireOp",VERTEX,"E7.center");
            var Q1;
            Q1=sQuery(id+"F0.wireOp",EDGE,"E4");
            cPlane(context, id + "F20", {"entities" : qUnion([Q0, Q1]), "cplaneType" : CPlaneType.LINE_POINT, "offset" : 25 * mm, "width" : 150 * mm, "height" : 150 * mm});
        }
        {
            var Q0;
            Q0=makeQuery(id+"F15.opExtrude","CAP_EDGE",EDGE,{"disambiguationData":[OSD([sQuery(id+"F0.wireOp",EDGE,"E7")])],"isStart":true});
            var Q1;
            Q1=makeQuery(id+"F15.opExtrude","CAP_EDGE",EDGE,{"disambiguationData":[OSD([sQuery(id+"F0.wireOp",EDGE,"E7")])],"isStart":false});
            chamfer(context, id + "F21", {"entities" : qUnion([Q0, Q1]), "width" : 1 * mm, "tangentPropagation" : true});
        }
        {
            var Q0;
            Q0=makeQuery(id+"F1.opExtrude","CAP_FACE",FACE,{"disambiguationData":[OSD([sQuery(id+"F0.wireOp",EDGE,"E0.bottom"),sQuery(id+"F0.wireOp",EDGE,"E0.top"),sQuery(id+"F0.wireOp",EDGE,"E0.left"),sQuery(id+"F0.wireOp",EDGE,"E0.right"),sQuery(id+"F0.wireOp",EDGE,"E1"),sQuery(id+"F0.wireOp",EDGE,"E30"),sQuery(id+"F0.wireOp",EDGE,"E31"),sQuery(id+"F0.wireOp",EDGE,"E32.MirrorCS"),sQuery(id+"F0.wireOp",EDGE,"E33.MirrorCS")])],"isStart":false});
            var sketch = newSketch(context, id + "F22", { "sketchPlane" : qUnion([Q0])});
            skLineSegment(sketch, "E84", {"start": v(6, 0) * mm, "end": v(6, -7.08) * mm});
            skLineSegment(sketch, "E85", {"start": v(6, -7.08) * mm, "end": v(-21.57, -7.08) * mm});
            skLineSegment(sketch, "E86", {"start": v(-21.57, -7.08) * mm, "end": v(-21.57, 13) * mm});
            skLineSegment(sketch, "E87", {"start": v(-21.57, 13) * mm, "end": v(0, 13) * mm});
            skLineSegment(sketch, "E88", {"start": v(0, 13) * mm, "end": v(0, 0) * mm});
            skLineSegment(sketch, "E89", {"start": v(0, 0) * mm, "end": v(6, 0) * mm});
            skLineSegment(sketch, "E90.MirrorCS", {"start": v(6, -7.08) * mm, "end": v(33.58, -7.08) * mm});
            skLineSegment(sketch, "E91.MirrorCS", {"start": v(33.58, -7.08) * mm, "end": v(33.58, 13) * mm});
            skLineSegment(sketch, "E92.MirrorCS", {"start": v(33.58, 13) * mm, "end": v(12, 13) * mm});
            skLineSegment(sketch, "E93.MirrorCS", {"start": v(12, 13) * mm, "end": v(12, 0) * mm});
            skSolve(sketch);
        }
        {
            var Q0;
            Q0=makeQuery(id+"F22.imprint","IMPRINT",FACE,{"disambiguationData":[TD([[makeQuery(id+"F22.imprint","IMPRINT",EDGE,{"derivedFrom":sQuery(id+"F22.wireOp",EDGE,"E84")}),-1.0]])]});
            var Q1;
            {var subQ1=sQuery(id+"F22.wireOp",EDGE,"E84");Q1=makeQuery(id+"F22.imprint","IMPRINT",FACE,{"disambiguationData":[TD([[makeQuery(id+"F22.imprint","IMPRINT",EDGE,{"derivedFrom":subQ1}),1.0]])]});}
            extrude(context, id + "F23", {"entities" : qUnion([Q0, Q1]), "oppositeDirection" : true, "depth" : 13 * mm, "offsetDistance" : 25 * mm});
        }
        {
            var Q0;
            Q0=makeQuery(id+"F23.opExtrude","SWEPT_FACE",FACE,{"disambiguationData":[OSD([sQuery(id+"F22.wireOp",EDGE,"E85"),sQuery(id+"F22.wireOp",EDGE,"E90.MirrorCS")])]});
            var sketch = newSketch(context, id + "F24", { "sketchPlane" : qUnion([Q0])});
            skLineSegment(sketch, "E94", {"start": v(400, -6) * mm, "end": v(387, -6) * mm, "construction": true});
            skCircle(sketch, "E95", {"center": v(393.5, -6) * mm, "radius": 1.44 * mm});
            skLineSegment(sketch, "E96", {"start": v(393.5, -6) * mm, "end": v(393.5, 15.17) * mm});
            skCircle(sketch, "E97", {"center": v(393.5, 15.17) * mm, "radius": 2.1 * mm});
            skLineSegment(sketch, "E98.MirrorCS", {"start": v(393.5, -6) * mm, "end": v(393.5, -27.17) * mm});
            skCircle(sketch, "E99.MirrorC", {"center": v(393.5, -27.17) * mm, "radius": 2.1 * mm});
            skSolve(sketch);
        }
        {
            var Q0;
            Q0=sQuery(id+"F24.wireOp",VERTEX,"vf1xUXdM-IFDV-wvwv-2arC-niVRvv8jzmKw.center");
            var Q1;
            Q1=sQuery(id+"F24.wireOp",VERTEX,"E95.center");
            var Q2;
            Q2=makeQuery(id+"F23.opExtrude","SWEPT_BODY",BODY,{"disambiguationData":[OSD([sQuery(id+"F0.wireOp",EDGE,"E0.bottom"),sQuery(id+"F22.wireOp",EDGE,"E85"),sQuery(id+"F22.wireOp",EDGE,"E86"),sQuery(id+"F22.wireOp",EDGE,"E87"),sQuery(id+"F22.wireOp",EDGE,"E88"),sQuery(id+"F22.wireOp",EDGE,"E89"),sQuery(id+"F22.wireOp",EDGE,"E90.MirrorCS"),sQuery(id+"F22.wireOp",EDGE,"E91.MirrorCS"),sQuery(id+"F22.wireOp",EDGE,"E92.MirrorCS"),sQuery(id+"F22.wireOp",EDGE,"E93.MirrorCS")])]});
            hole(context, id + "F25", {"style" : HoleStyle.C_BORE, "endStyle" : HoleEndStyle.THROUGH, "holeDiameter" : 3.6 * mm, "cBoreDiameter" : 9 * mm, "cBoreDepth" : 4 * mm, "majorDiameter" : 5 * mm, "isTappedThrough" : true, "tappedDepth" : 12 * mm, "tapClearance" : 3, "locations" : qUnion([Q0, Q1]), "scope" : qUnion([Q2])});
        }
        {
            var Q0;
            Q0=sQuery(id+"F24.wireOp",VERTEX,"E97.center");
            var Q1;
            Q1=sQuery(id+"F24.wireOp",VERTEX,"E98.MirrorCS.end");
            var Q2;
            Q2=makeQuery(id+"F23.opExtrude","SWEPT_BODY",BODY,{"disambiguationData":[OSD([sQuery(id+"F0.wireOp",EDGE,"E0.bottom"),sQuery(id+"F22.wireOp",EDGE,"E85"),sQuery(id+"F22.wireOp",EDGE,"E86"),sQuery(id+"F22.wireOp",EDGE,"E87"),sQuery(id+"F22.wireOp",EDGE,"E88"),sQuery(id+"F22.wireOp",EDGE,"E89"),sQuery(id+"F22.wireOp",EDGE,"E90.MirrorCS"),sQuery(id+"F22.wireOp",EDGE,"E91.MirrorCS"),sQuery(id+"F22.wireOp",EDGE,"E92.MirrorCS"),sQuery(id+"F22.wireOp",EDGE,"E93.MirrorCS")])]});
            hole(context, id + "F26", {"style" : HoleStyle.C_BORE, "endStyle" : HoleEndStyle.THROUGH, "holeDiameter" : 3.6 * mm, "cBoreDiameter" : 9 * mm, "cBoreDepth" : 17 * mm, "majorDiameter" : 5 * mm, "isTappedThrough" : true, "tappedDepth" : 12 * mm, "tapClearance" : 3, "locations" : qUnion([Q0, Q1]), "scope" : qUnion([Q2])});
        }
    });
